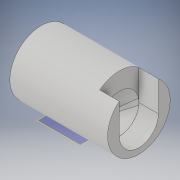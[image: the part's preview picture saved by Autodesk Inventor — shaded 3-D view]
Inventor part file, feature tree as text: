
AUTODESK INVENTOR PART (.ipt)
format: ipt  version: 2019 (Build 230136000, 136)  size: 251,904 bytes
history: native  units: in
note: dims shown in document units (in); Inventor stores cm internally (conversion verified against a paired STEP export)
features: sketch x8, extrude x3, revolve x1, loft x1, fillet x1, plane x1, other x1
ambient origin geometry x8: Origin, YZ Plane, XZ Plane, XY Plane, X Axis, Y Axis, Z Axis, Center Point
bodies: Solid1 (feature_tree)
feature tree (16):
  revolve  "Revolution1"  [1 undecoded]
  sketch  "Sketch2"  dims[d3=0.7874in d4=90.0deg]
  extrude  "Extrusion1"  TaperAngle=90.0deg  [1 undecoded]
  sketch  "Sketch4"  dims[d9=0.7874in d10=0.0in d11=90.0deg]
  sketch  "Sketch5"  dims[d12=0.0in d13=90.0deg d14=0.2362in]
  loft  "Loft1"
  fillet  "Fillet1"  Radius=0.3937in
  sketch  "Sketch6"  dims[d15=0.5118in]
  plane  "Work Plane1"
  extrude  "Extrusion2"  TaperAngle=0.0deg  [1 undecoded]
  extrude  "Extrusion3"  Depth=0.2362in
  sketch  "Sketch1"  dims[d0=0.1181in d1=0.7874in]
  sketch  "Sketch3"  dims[d5=0.0591in d6=0.5118in d7=0.3937in d8=0.0in]
  other  "Edges1"
  sketch  "Sketch7"  dims[d16=0.1969in d17=0.0in]
  sketch  "Sketch8"  dims[d18=0.6299in d19=0.7177in d22=0.3937in d24=0.3937in d25=0.0in]
note: 3 required parameter values undecoded (feature->parameter linkage not recoverable at this tier; creation-order binding heuristic only, values carry confidence <= 0.55)